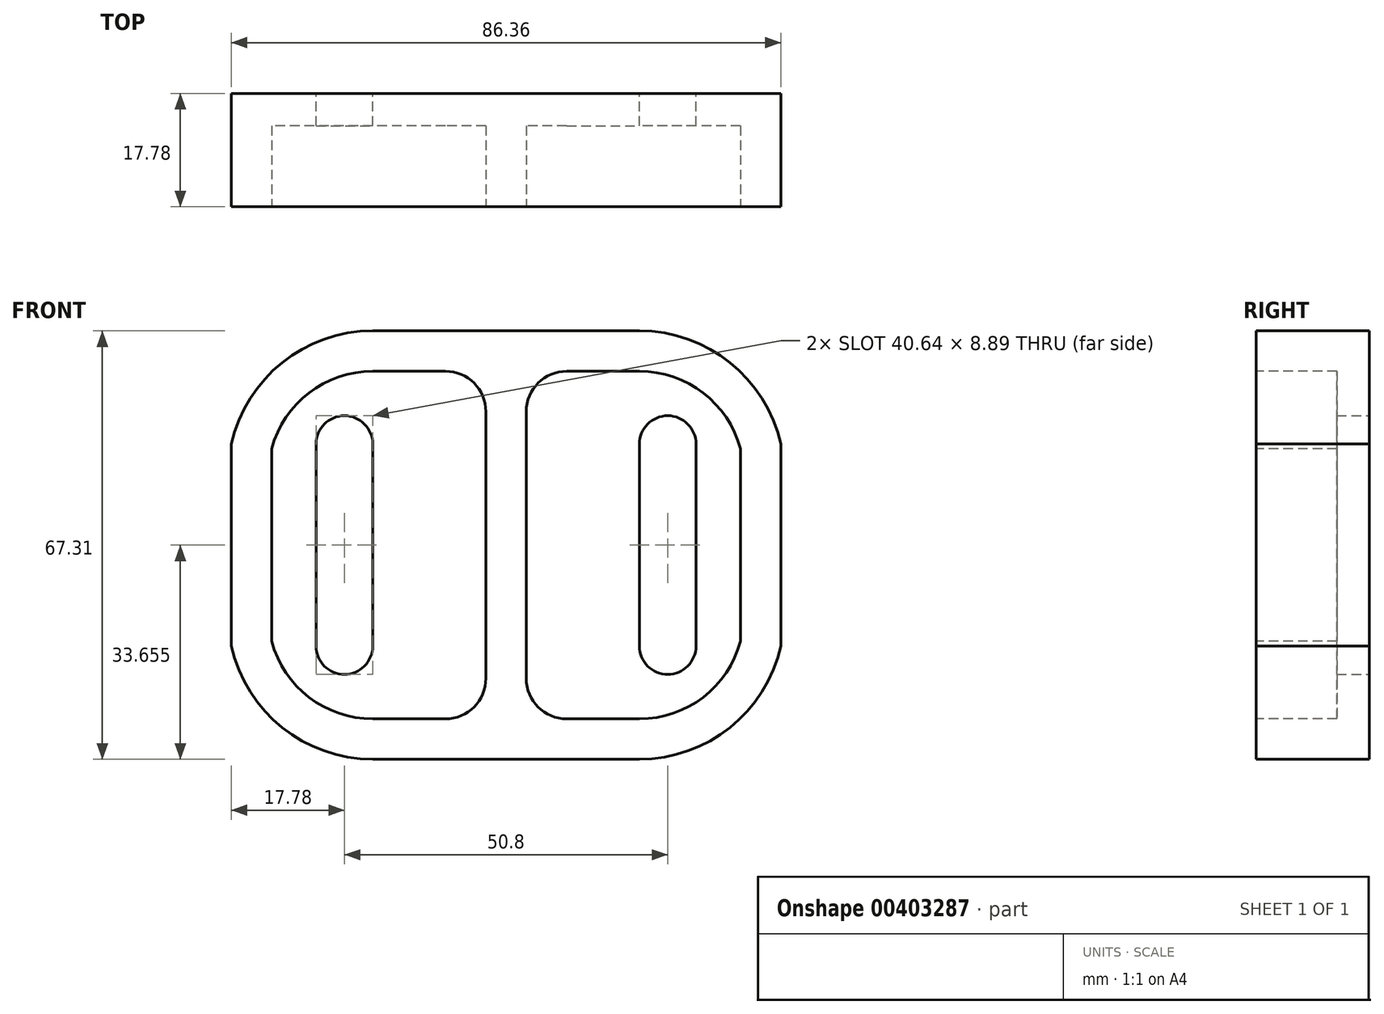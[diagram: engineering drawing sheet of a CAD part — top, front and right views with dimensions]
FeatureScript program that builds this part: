
annotation { "Feature Type Name" : "Feature", "Feature Type Description" : "" }
export const myFeature = defineFeature(function(context is Context, id is Id, definition is map)
    precondition{}
    {
        {
            var Q0;
            Q0=qCreatedBy(makeId("Front.planeOp"),FACE);
            var sketch = newSketch(context, id + "F0", { "sketchPlane" : qUnion([Q0])});
            skArc(sketch, "E0.0.startCap", {"start": v(-20.96, 17.78) * mm, "mid": v(-25.4, 13.33) * mm, "end": v(-29.85, 17.78) * mm});
            skArc(sketch, "E0.0.endCap", {"start": v(-29.84, 49.53) * mm, "mid": v(-25.4, 53.98) * mm, "end": v(-20.95, 49.53) * mm});
            skLineSegment(sketch, "E0.0.left", {"start": v(-29.85, 17.78) * mm, "end": v(-29.85, 49.53) * mm});
            skLineSegment(sketch, "E0.0.right", {"start": v(-20.96, 17.78) * mm, "end": v(-20.96, 49.53) * mm});
            skArc(sketch, "E1", {"start": v(-43.18, 17.78) * mm, "mid": v(-35.19, 5) * mm, "end": v(-20.96, 0) * mm});
            skLineSegment(sketch, "E2", {"start": v(-20.96, 0) * mm, "end": v(0, 0) * mm});
            skPoint(sketch, "E3", {"position": v(-20.96, 33.66) * mm});
            skLineSegment(sketch, "E4", {"start": v(-43.18, 17.78) * mm, "end": v(-43.18, 33.66) * mm});
            skLineSegment(sketch, "E5", {"start": v(-43.18, 33.66) * mm, "end": v(-29.85, 33.66) * mm, "construction": true});
            skLineSegment(sketch, "E6.MirrorCS", {"start": v(-20.96, 67.31) * mm, "end": v(0, 67.31) * mm});
            skLineSegment(sketch, "E7.MirrorCS", {"start": v(-43.18, 49.53) * mm, "end": v(-43.18, 33.66) * mm});
            skArc(sketch, "E8.MirrorCS", {"start": v(-43.18, 49.53) * mm, "mid": v(-35.19, 62.32) * mm, "end": v(-20.96, 67.31) * mm});
            skArc(sketch, "E9.MirrorCS", {"start": v(-29.85, 17.78) * mm, "mid": v(-25.4, 13.33) * mm, "end": v(-20.96, 17.78) * mm});
            skLineSegment(sketch, "E10.MirrorCS", {"start": v(-29.85, 49.53) * mm, "end": v(-29.85, 17.78) * mm});
            skLineSegment(sketch, "E11.MirrorCS", {"start": v(-20.96, 49.53) * mm, "end": v(-20.96, 17.78) * mm});
            skArc(sketch, "E12.MirrorCS", {"start": v(-20.95, 49.53) * mm, "mid": v(-25.4, 53.98) * mm, "end": v(-29.84, 49.53) * mm});
            skArc(sketch, "E13.MirrorCS", {"start": v(-20.96, 17.78) * mm, "mid": v(-25.4, 13.34) * mm, "end": v(-29.85, 17.78) * mm});
            skLineSegment(sketch, "E14.MirrorCS", {"start": v(20.96, 0) * mm, "end": v(0, 0) * mm});
            skArc(sketch, "E15.MirrorCS", {"start": v(43.18, 17.78) * mm, "mid": v(35.19, 5) * mm, "end": v(20.96, 0) * mm});
            skLineSegment(sketch, "E16.MirrorCS", {"start": v(43.18, 49.53) * mm, "end": v(43.18, 33.66) * mm});
            skLineSegment(sketch, "E17.MirrorCS", {"start": v(43.18, 17.78) * mm, "end": v(43.18, 33.66) * mm});
            skArc(sketch, "E18.MirrorCS", {"start": v(43.18, 49.53) * mm, "mid": v(35.19, 62.32) * mm, "end": v(20.96, 67.3) * mm});
            skLineSegment(sketch, "E19.MirrorCS", {"start": v(20.96, 67.31) * mm, "end": v(0, 67.31) * mm});
            skArc(sketch, "E20.MirrorCS", {"start": v(20.95, 49.53) * mm, "mid": v(25.4, 53.98) * mm, "end": v(29.84, 49.53) * mm});
            skLineSegment(sketch, "E21.MirrorCS", {"start": v(20.96, 17.78) * mm, "end": v(20.96, 49.53) * mm});
            skLineSegment(sketch, "E22.MirrorCS", {"start": v(29.85, 17.78) * mm, "end": v(29.84, 49.53) * mm});
            skArc(sketch, "E23.MirrorCS", {"start": v(20.96, 17.78) * mm, "mid": v(25.4, 13.34) * mm, "end": v(29.85, 17.78) * mm});
            skLineSegment(sketch, "E24", {"start": v(-25.4, 17.78) * mm, "end": v(-25.4, 49.53) * mm, "construction": true});
            skCircle(sketch, "E25", {"center": v(-25.4, 17.78) * mm, "radius": 8.9 * mm, "construction": true});
            skSolve(sketch);
        }
        {
            var Q0;
            Q0 = qSketchRegion(id + "F0", true);
            extrude(context, id + "F1", {"entities" : qUnion([Q0]), "depth" : 17.78 * mm});
        }
        {
            var Q0;
            Q0=makeQuery(id+"F1.opExtrude","CAP_FACE",FACE,{"disambiguationData":[OSD([sQuery(id+"F0.wireOp",EDGE,"E0.0.right"),sQuery(id+"F0.wireOp",EDGE,"E7.MirrorCS"),sQuery(id+"F0.wireOp",EDGE,"E2"),sQuery(id+"F0.wireOp",EDGE,"E13.MirrorCS"),sQuery(id+"F0.wireOp",EDGE,"E1"),sQuery(id+"F0.wireOp",EDGE,"E4"),sQuery(id+"F0.wireOp",EDGE,"E8.MirrorCS"),sQuery(id+"F0.wireOp",EDGE,"E10.MirrorCS"),sQuery(id+"F0.wireOp",EDGE,"E6.MirrorCS"),sQuery(id+"F0.wireOp",EDGE,"E12.MirrorCS"),sQuery(id+"F0.wireOp",EDGE,"E14.MirrorCS"),sQuery(id+"F0.wireOp",EDGE,"E15.MirrorCS"),sQuery(id+"F0.wireOp",EDGE,"E16.MirrorCS"),sQuery(id+"F0.wireOp",EDGE,"E17.MirrorCS"),sQuery(id+"F0.wireOp",EDGE,"E18.MirrorCS"),sQuery(id+"F0.wireOp",EDGE,"E19.MirrorCS"),sQuery(id+"F0.wireOp",EDGE,"E20.MirrorCS"),sQuery(id+"F0.wireOp",EDGE,"E21.MirrorCS"),sQuery(id+"F0.wireOp",EDGE,"E22.MirrorCS"),sQuery(id+"F0.wireOp",EDGE,"E23.MirrorCS")])],"isStart":false});
            var sketch = newSketch(context, id + "F2", { "sketchPlane" : qUnion([Q0])});
            skLineSegment(sketch, "E26", {"start": v(0, 67.31) * mm, "end": v(0, 0) * mm, "construction": true});
            skLineSegment(sketch, "E27.0", {"start": v(-20.96, 6.35) * mm, "end": v(-9.52, 6.35) * mm});
            skLineSegment(sketch, "E27.1", {"start": v(-9.53, 60.96) * mm, "end": v(-20.96, 60.96) * mm});
            skArc(sketch, "E27.2", {"start": v(-36.83, 48.77) * mm, "mid": v(-30.96, 57.56) * mm, "end": v(-20.96, 60.96) * mm});
            skLineSegment(sketch, "E27.3", {"start": v(-36.83, 48.77) * mm, "end": v(-36.83, 18.54) * mm});
            skArc(sketch, "E27.4", {"start": v(-36.83, 18.54) * mm, "mid": v(-30.96, 9.75) * mm, "end": v(-20.96, 6.35) * mm});
            skLineSegment(sketch, "E28", {"start": v(-3.18, 54.61) * mm, "end": v(-3.17, 12.7) * mm});
            skPoint(sketch, "E29.orphan", {"position": v(0, 60.96) * mm});
            skPoint(sketch, "E30.orphan", {"position": v(0, 6.35) * mm});
            skPoint(sketch, "E31.visualSharp", {"position": v(-3.18, 60.96) * mm});
            skArc(sketch, "E31.filletArc", {"start": v(-3.18, 54.61) * mm, "mid": v(-5.03, 59.1) * mm, "end": v(-9.53, 60.96) * mm});
            skPoint(sketch, "E32.visualSharp", {"position": v(-3.17, 6.35) * mm});
            skArc(sketch, "E32.filletArc", {"start": v(-9.52, 6.35) * mm, "mid": v(-5.03, 8.2) * mm, "end": v(-3.17, 12.7) * mm});
            skLineSegment(sketch, "E33.MirrorCS", {"start": v(9.53, 60.96) * mm, "end": v(20.96, 60.96) * mm});
            skArc(sketch, "E34.MirrorCS", {"start": v(36.83, 48.77) * mm, "mid": v(30.96, 57.56) * mm, "end": v(20.96, 60.96) * mm});
            skPoint(sketch, "E35.MirrorP", {"position": v(3.18, 60.96) * mm});
            skArc(sketch, "E36.MirrorCS", {"start": v(3.18, 54.61) * mm, "mid": v(5.03, 59.1) * mm, "end": v(9.53, 60.96) * mm});
            skPoint(sketch, "E37.MirrorP", {"position": v(3.17, 6.35) * mm});
            skLineSegment(sketch, "E38.MirrorCS", {"start": v(3.18, 54.61) * mm, "end": v(3.17, 12.7) * mm});
            skArc(sketch, "E39.MirrorCS", {"start": v(36.83, 18.54) * mm, "mid": v(30.96, 9.75) * mm, "end": v(20.96, 6.35) * mm});
            skArc(sketch, "E40.MirrorCS", {"start": v(9.52, 6.35) * mm, "mid": v(5.03, 8.2) * mm, "end": v(3.17, 12.7) * mm});
            skLineSegment(sketch, "E41.MirrorCS", {"start": v(36.83, 48.77) * mm, "end": v(36.83, 18.54) * mm});
            skLineSegment(sketch, "E42.MirrorCS", {"start": v(20.96, 6.35) * mm, "end": v(9.52, 6.35) * mm});
            skSolve(sketch);
        }
        {
            var Q0;
            Q0 = qSketchRegion(id + "F2", true);
            extrude(context, id + "F3", {"entities" : qUnion([Q0]), "operationType" : NewBodyOperationType.REMOVE, "oppositeDirection" : true, "depth" : 12.7 * mm});
        }
    });
